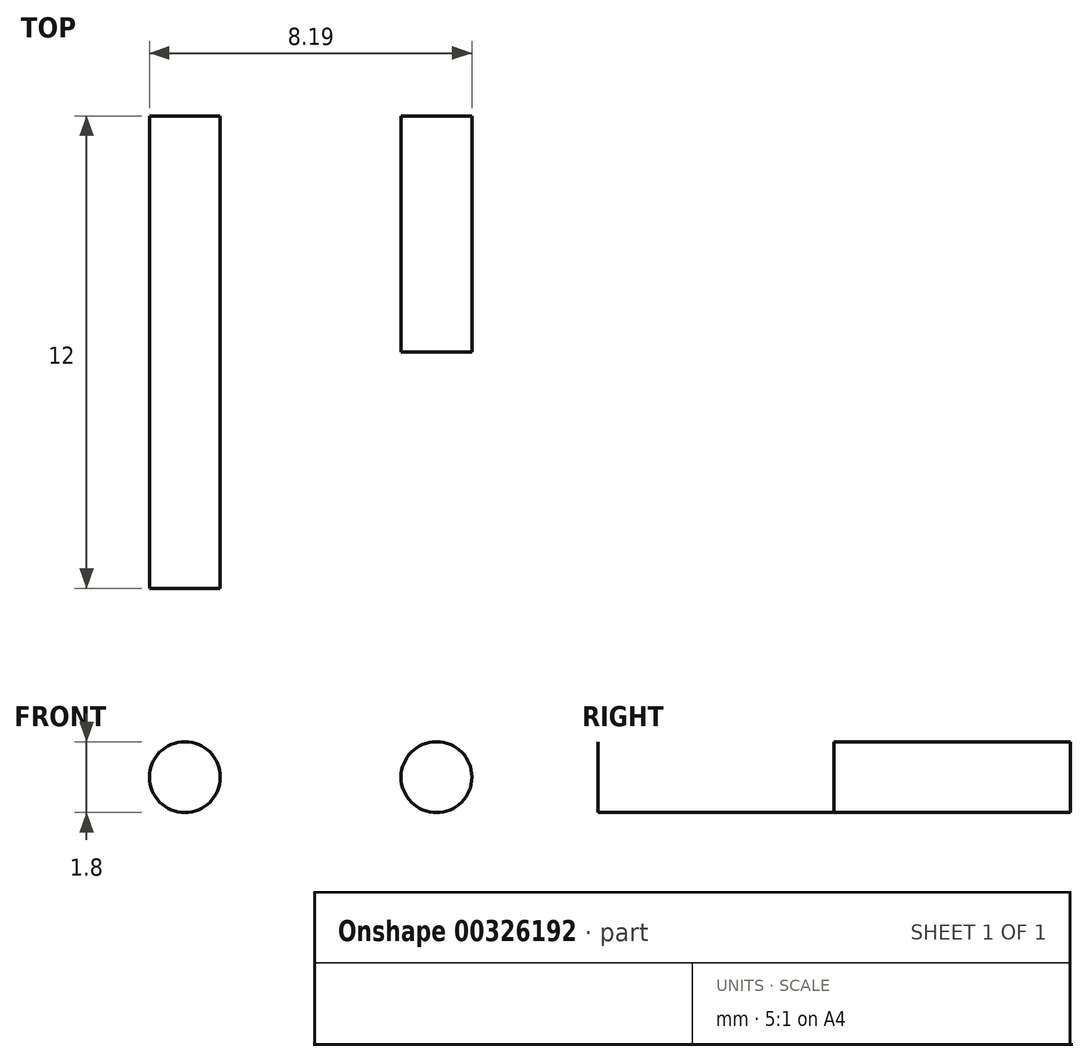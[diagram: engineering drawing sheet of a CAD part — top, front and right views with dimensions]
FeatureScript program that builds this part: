
annotation { "Feature Type Name" : "Feature", "Feature Type Description" : "" }
export const myFeature = defineFeature(function(context is Context, id is Id, definition is map)
    precondition{}
    {
        {
            var Q0;
            Q0=qCreatedBy(makeId("Front.planeOp"),FACE);
            var sketch = newSketch(context, id + "F0", { "sketchPlane" : qUnion([Q0])});
            skCircle(sketch, "E0", {"center": v(0, 0) * mm, "radius": 0.9 * mm});
            skCircle(sketch, "E1", {"center": v(-6.4, 0) * mm, "radius": 0.9 * mm});
            skSolve(sketch);
        }
        {
            var Q0;
            Q0 = qSketchRegion(id + "F0", true);
            extrude(context, id + "F1", {"entities" : qUnion([Q0]), "depth" : 6 * mm});
        }
        {
            var Q0;
            Q0=makeQuery(id+"F1.opExtrude","CAP_FACE",FACE,{"disambiguationData":[OSD([sQuery(id+"F0.wireOp",EDGE,"E1")])],"isStart":false});
            extrude(context, id + "F2", {"entities" : qUnion([Q0]), "operationType" : NewBodyOperationType.ADD, "depth" : 6 * mm});
        }
    });
